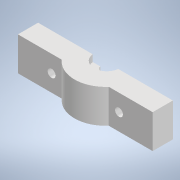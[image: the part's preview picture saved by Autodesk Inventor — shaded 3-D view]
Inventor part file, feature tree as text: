
AUTODESK INVENTOR PART (.ipt)
format: ipt  version: 2020.2 (Build 242310000, 310)  size: 134,656 bytes
history: native  units: mm
features: sketch x5, extrude x4, hole x1
ambient origin geometry x8: Origin, YZ Plane, XZ Plane, XY Plane, X Axis, Y Axis, Z Axis, Center Point
bodies: Solido1 (feature_tree)
feature tree (10):
  extrude  "Estrusione1"  Depth=100.0mm
  extrude  "Estrusione2"  Depth=25.0mm
  extrude  "Estrusione3"  Depth=15.0mm TaperAngle=0.0deg
  hole  "Foro1"  [1 undecoded]
  extrude  "Estrusione4"  TaperAngle=90.0deg  [1 undecoded]
  sketch  "Schizzo1"
  sketch  "Schizzo2"
  sketch  "Schizzo3"
  sketch  "Schizzo4"
  sketch  "Schizzo5"
note: 2 required parameter values undecoded (feature->parameter linkage not recoverable at this tier; creation-order binding heuristic only, values carry confidence <= 0.55)
